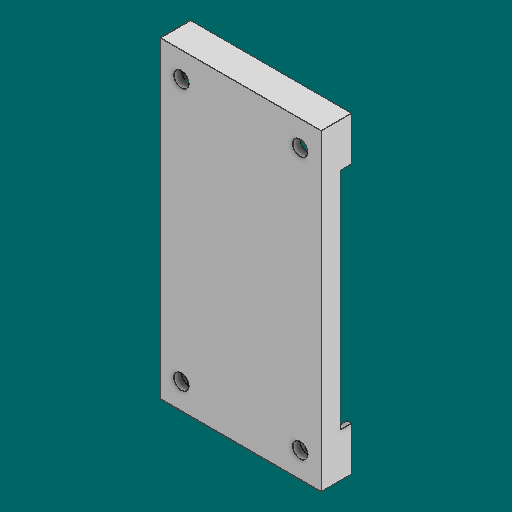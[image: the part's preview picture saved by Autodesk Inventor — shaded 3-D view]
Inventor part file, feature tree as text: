
AUTODESK INVENTOR PART (.ipt)
format: ipt  version: 2025.2 (Build 292293000, 293)  size: 133,632 bytes
history: native  units: mm
features: reference x7, sketch x4, extrude x3, other x2, plane x1
ambient origin geometry x8: Origin, YZ Plane, XZ Plane, XY Plane, X Axis, Y Axis, Z Axis, Center Point
bodies: Solid1 (feature_tree)
feature tree (17):
  plane  "Work Plane1"
  extrude  "Extrusion1"  Depth=203.0mm
  extrude  "Extrusion2"  Depth=5.0mm TaperAngle=0.0deg
  sketch  "Sketch3"  dims[d5=3.0mm d6=15.0mm d7=0.0mm]
  extrude  "Extrusion3"  Depth=15.0mm TaperAngle=0.0deg
  sketch  "Sketch1"  dims[d0=106.0mm d1=203.0mm]
  reference  "Reference1"
  reference  "Reference2"
  reference  "Reference3"
  reference  "Reference4"
  reference  "Reference5"
  sketch  "Sketch2"  dims[d2=3.0mm d3=5.0mm d4=0.0mm]
  sketch  "Sketch4"  dims[d8=15.0mm d9=0.0mm]
  reference  "Reference6"
  reference  "Reference7"
  other  "CassingHardware.iam"
  other  "atas:1"
